# Revit family: Haworth_Epure_CompactDesk_Symmetrical120_EU_PRELIMINARY
name_source: partatom
category: Furniture
units: mm (PartAtom-declared; Revit-internal decimal feet)

## family parameters
Always vertical = Yes
Cut with Voids When Loaded = No
OmniClass Number = 23.40.70.14.64.11
OmniClass Title = Office Furniture
Room Calculation Point = No
Shared = No
Work Plane-Based = No

## types (4) — shared parameters
120w x 120deg - rounded = No
140w x 120deg - rounded = No
Actual Height = 73 cm
Assembly Code = E2020200
Description = Haworth - Epure - Symmetrical Compact Desk
Flip Top Finish = Haworth _ Paint _ Metallic Silver
Leg Height = 70 cm
Manufacturer = Haworth
Model = EUCOXXXXX
Revision Number = 1
Rounded Corners = No
Size = Verify Final Dim.w/ Haworth
Squared Corners = Yes
Trim Finish = Haworth _ Metal _ Structured White EC
URL = https://www.haworth.com
URL - Product = https://www.haworth.com
Warranty = http://www.haworth.com

## per-type parameters (varying)
| type | Accessory Kit | Actual Depth | Actual Width | Cable Outlet 120w | Cable Outlet 140w | Flip Top Cable Outlet | Large | Leg Width | No Accessory Kit | Small |
| 120w x 120deg - squared | No | 120 cm | 120 cm | No | No | No | No | 0 cm | Yes | Yes |
| 140w x 120deg - squared | No | 140 cm | 140 cm | No | No | No | Yes | 22 cm | Yes | No |
| 120w x 120deg - rounded | Yes | 120 cm | 120 cm | Yes | No | Yes | No | 0 cm | No | Yes |
| 140w x 120deg - rounded | Yes | 140 cm | 140 cm | No | Yes | Yes | Yes | 22 cm | No | No |

type visibility flags (boolean, named after types; folded from table):
- 120w x 120deg - squared: Yes: 120w x 120deg - squared
- 140w x 120deg - squared: Yes: 140w x 120deg - squared
- 120w x 120deg - rounded: Yes: 120w x 120deg - squared
- 140w x 120deg - rounded: Yes: 140w x 120deg - squared

## geometry (parser evidence)
native form markers: Sweep x13
no freeform markers — native parametric forms only
